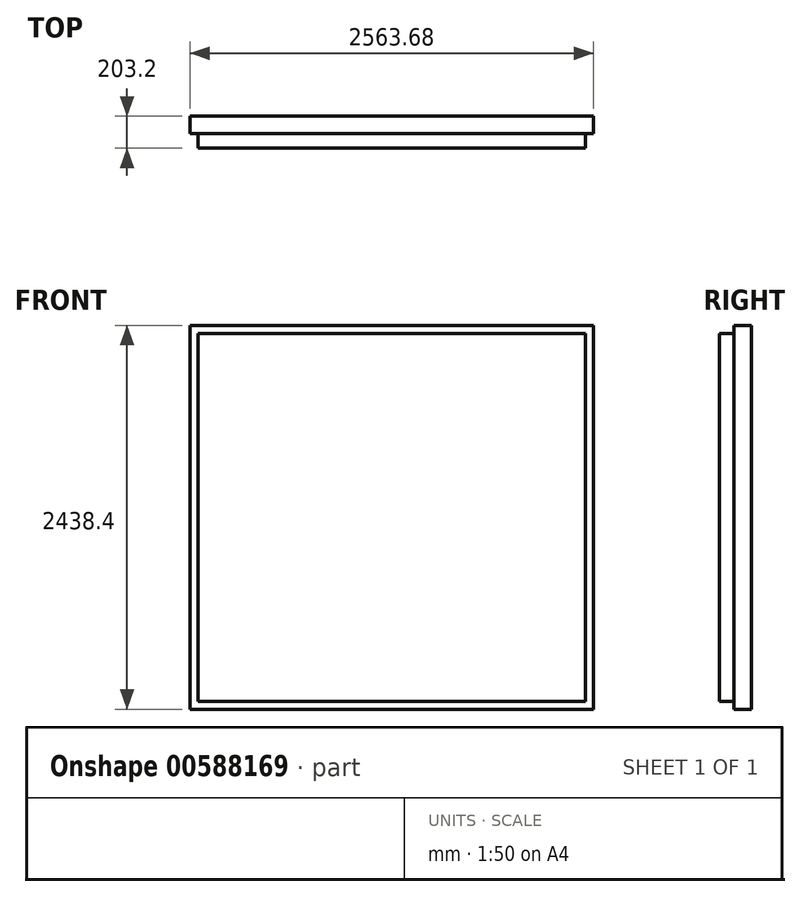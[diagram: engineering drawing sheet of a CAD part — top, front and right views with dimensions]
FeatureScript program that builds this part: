
annotation { "Feature Type Name" : "Feature", "Feature Type Description" : "" }
export const myFeature = defineFeature(function(context is Context, id is Id, definition is map)
    precondition{}
    {
        {
            var Q0;
            Q0=qCreatedBy(makeId("Top.planeOp"),FACE);
            var sketch = newSketch(context, id + "F0", { "sketchPlane" : qUnion([Q0])});
            skLineSegment(sketch, "E0.bottom", {"start": v(-52.48, 56.91) * mm, "end": v(72.8, 56.91) * mm});
            skLineSegment(sketch, "E0.top", {"start": v(-52.48, 66.15) * mm, "end": v(72.8, 66.15) * mm});
            skLineSegment(sketch, "E0.left", {"start": v(-52.48, 56.91) * mm, "end": v(-52.48, 66.15) * mm});
            skLineSegment(sketch, "E0.right", {"start": v(72.8, 56.91) * mm, "end": v(72.8, 66.15) * mm});
            skSolve(sketch);
        }
        {
            var Q0;
            Q0=makeQuery(id+"F0.imprint","IMPRINT",FACE,{"disambiguationData":[TD([[makeQuery(id+"F0.imprint","IMPRINT",EDGE,{"derivedFrom":sQuery(id+"F0.wireOp",EDGE,"E0.bottom")}),1.0]])]});
            extrude(context, id + "F1", {"entities" : qUnion([Q0]), "depth" : 2438.4 * mm, "offsetDistance" : 25.4 * mm});
        }
        {
            var Q0;
            Q0=makeQuery(id+"F1.opExtrude","SWEPT_FACE",FACE,{"disambiguationData":[OSD([sQuery(id+"F0.wireOp",EDGE,"E0.left")])]});
            extrude(context, id + "F2", {"entities" : qUnion([Q0]), "operationType" : NewBodyOperationType.ADD, "depth" : 2438.4 * mm, "offsetDistance" : 25.4 * mm});
        }
        {
            var Q0;
            {var subQ0=sQuery(id+"F0.wireOp",EDGE,"E0.top");Q0=makeQuery(id+"F2.boolean.opBoolean","MERGE",FACE,{"derivedFrom":[makeQuery(id+"F1.opExtrude","SWEPT_FACE",FACE,{"disambiguationData":[OSD([subQ0])]}),makeQuery(id+"F2.opExtrude","SWEPT_FACE",FACE,{"disambiguationData":[OSD([subQ0,sQuery(id+"F0.wireOp",EDGE,"E0.left")])]})]});}
            extrude(context, id + "F3", {"entities" : qUnion([Q0]), "operationType" : NewBodyOperationType.ADD, "depth" : 101.6 * mm, "offsetDistance" : 25.4 * mm});
        }
        {
            var Q0;
            {var subQ0=sQuery(id+"F0.wireOp",EDGE,"E0.bottom");Q0=makeQuery(id+"F2.boolean.opBoolean","MERGE",FACE,{"derivedFrom":[makeQuery(id+"F1.opExtrude","SWEPT_FACE",FACE,{"disambiguationData":[OSD([subQ0])]}),makeQuery(id+"F2.opExtrude","SWEPT_FACE",FACE,{"disambiguationData":[OSD([subQ0,sQuery(id+"F0.wireOp",EDGE,"E0.left")])]})]});}
            shell(context, id + "F4", {"entities" : qUnion([Q0]), "thickness" : 50.8 * mm});
        }
        {
            var Q0;
            {var subQ0=sQuery(id+"F0.wireOp",EDGE,"E0.left");var subQ1=sQuery(id+"F0.wireOp",EDGE,"E0.top");Q0=makeQuery(id+"F4.opShell","OFFSET_FACE",FACE,{"disambiguationData":[OSD([subQ1,subQ0]),TDD([makeQuery(id+"F3.opExtrude","CAP_FACE",FACE,{"disambiguationData":[OSD([subQ1,subQ0])],"isStart":false})])]});}
            extrude(context, id + "F5", {"entities" : qUnion([Q0]), "operationType" : NewBodyOperationType.ADD, "depth" : 152.4 * mm, "offsetDistance" : 25.4 * mm});
        }
    });
